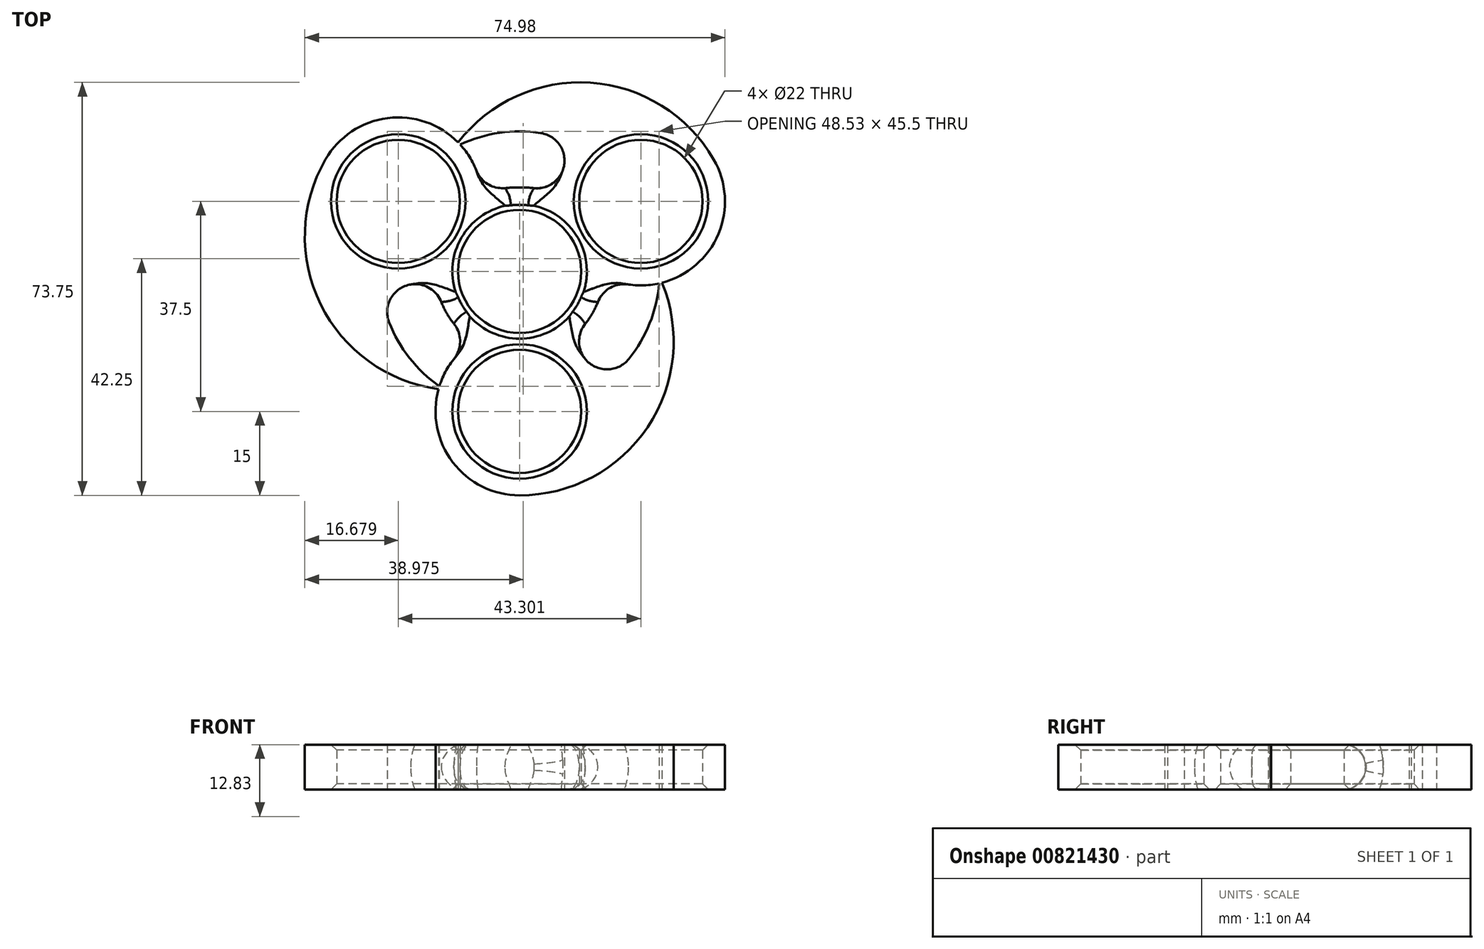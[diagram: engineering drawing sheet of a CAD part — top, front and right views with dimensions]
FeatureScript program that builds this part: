
annotation { "Feature Type Name" : "Feature", "Feature Type Description" : "" }
export const myFeature = defineFeature(function(context is Context, id is Id, definition is map)
    precondition{}
    {
        {
            var Q0;
            Q0=qCreatedBy(makeId("Top.planeOp"),FACE);
            var sketch = newSketch(context, id + "F0", { "sketchPlane" : qUnion([Q0])});
            skCircle(sketch, "E0", {"center": v(0, 0) * mm, "radius": 15 * mm});
            skCircle(sketch, "E1", {"center": v(0, 0) * mm, "radius": 25 * mm, "construction": true});
            skLineSegment(sketch, "E2", {"start": v(0, 56.43) * mm, "end": v(0, 0) * mm});
            skLineSegment(sketch, "E3", {"start": v(0, 0) * mm, "end": v(21.65, 12.5) * mm});
            skLineSegment(sketch, "E4", {"start": v(0, 0) * mm, "end": v(-21.65, 12.5) * mm});
            skLineSegment(sketch, "E5", {"start": v(0, 0) * mm, "end": v(0, -25) * mm});
            skCircle(sketch, "E6", {"center": v(-21.65, 12.5) * mm, "radius": 11 * mm});
            skCircle(sketch, "E7", {"center": v(21.65, 12.5) * mm, "radius": 11 * mm});
            skCircle(sketch, "E8", {"center": v(0, -25) * mm, "radius": 11 * mm});
            skCircle(sketch, "E9", {"center": v(-21.65, 12.5) * mm, "radius": 15 * mm});
            skCircle(sketch, "E10", {"center": v(21.65, 12.5) * mm, "radius": 15 * mm});
            skCircle(sketch, "E11", {"center": v(0, -25) * mm, "radius": 15 * mm});
            skCircle(sketch, "E12", {"center": v(0, 0) * mm, "radius": 11 * mm});
            skCircle(sketch, "E13", {"center": v(-10.83, 6.25) * mm, "radius": 27.5 * mm});
            skCircle(sketch, "E14", {"center": v(10.83, 6.25) * mm, "radius": 27.5 * mm});
            skCircle(sketch, "E15", {"center": v(0, -12.5) * mm, "radius": 27.5 * mm});
            skCircle(sketch, "E16", {"center": v(0, 15) * mm, "radius": 32.8 * mm});
            skCircle(sketch, "E17", {"center": v(0, -15) * mm, "radius": 46 * mm});
            skCircle(sketch, "E18", {"center": v(12.12, 7) * mm, "radius": 45.22 * mm});
            skCircle(sketch, "E19", {"center": v(0, 0) * mm, "radius": 25 * mm});
            skSolve(sketch);
        }
        {
            var Q0;
            {var subQ3=sQuery(id+"F0.wireOp",EDGE,"E19");var subQ6=sQuery(id+"F0.wireOp",EDGE,"E8");var subQ9=makeQuery(id+"F0.imprint","INTERSECT",VERTEX,{"disambiguationData":[OD(1.0)],"derivedFrom":[subQ6,subQ3]});Q0=makeQuery(id+"F0.imprint","IMPRINT",FACE,{"disambiguationData":[TD([[makeQuery(id+"F0.imprint","IMPRINT",EDGE,{"disambiguationData":[TD([[subQ9,-1.0]])],"derivedFrom":subQ6}),-1.0]])]});}
            var Q1;
            {var subQ0=sQuery(id+"F0.wireOp",EDGE,"E13");var subQ1=sQuery(id+"F0.wireOp",EDGE,"E8");var subQ2=makeQuery(id+"F0.imprint","INTERSECT",VERTEX,{"disambiguationData":[OD(1.0)],"derivedFrom":[subQ1,subQ0]});Q1=makeQuery(id+"F0.imprint","IMPRINT",FACE,{"disambiguationData":[TD([[makeQuery(id+"F0.imprint","IMPRINT",EDGE,{"disambiguationData":[TD([[subQ2,-1.0]])],"derivedFrom":subQ1}),-1.0]])]});}
            var Q2;
            {var subQ0=sQuery(id+"F0.wireOp",EDGE,"E16");var subQ1=sQuery(id+"F0.wireOp",EDGE,"E8");var subQ2=makeQuery(id+"F0.imprint","INTERSECT",VERTEX,{"disambiguationData":[OD(1.0)],"derivedFrom":[subQ1,subQ0]});Q2=makeQuery(id+"F0.imprint","IMPRINT",FACE,{"disambiguationData":[TD([[makeQuery(id+"F0.imprint","IMPRINT",EDGE,{"disambiguationData":[TD([[subQ2,-1.0]])],"derivedFrom":subQ1}),-1.0]])]});}
            var Q3;
            {var subQ0=sQuery(id+"F0.wireOp",EDGE,"E19");var subQ1=sQuery(id+"F0.wireOp",EDGE,"E11");var subQ2=makeQuery(id+"F0.imprint","INTERSECT",VERTEX,{"disambiguationData":[OD(1.0)],"derivedFrom":[subQ1,subQ0]});Q3=makeQuery(id+"F0.imprint","IMPRINT",FACE,{"disambiguationData":[TD([[makeQuery(id+"F0.imprint","IMPRINT",EDGE,{"disambiguationData":[TD([[subQ2,-1.0]])],"derivedFrom":subQ1}),1.0]])]});}
            var Q4;
            {var subQ0=sQuery(id+"F0.wireOp",EDGE,"E14");var subQ1=sQuery(id+"F0.wireOp",EDGE,"E8");var subQ2=makeQuery(id+"F0.imprint","INTERSECT",VERTEX,{"disambiguationData":[OD(1.0)],"derivedFrom":[subQ1,subQ0]});Q4=makeQuery(id+"F0.imprint","IMPRINT",FACE,{"disambiguationData":[TD([[makeQuery(id+"F0.imprint","IMPRINT",EDGE,{"disambiguationData":[TD([[subQ2,-1.0]])],"derivedFrom":subQ1}),-1.0]])]});}
            var Q5;
            {var subQ0=sQuery(id+"F0.wireOp",EDGE,"E11");var subQ1=sQuery(id+"F0.wireOp",EDGE,"E0");var subQ2=makeQuery(id+"F0.imprint","INTERSECT",VERTEX,{"disambiguationData":[OD(0.0)],"derivedFrom":[subQ1,subQ0]});Q5=makeQuery(id+"F0.imprint","IMPRINT",FACE,{"disambiguationData":[TD([[makeQuery(id+"F0.imprint","IMPRINT",EDGE,{"disambiguationData":[TD([[subQ2,-1.0]])],"derivedFrom":subQ1}),-1.0]])]});}
            var Q6;
            {var subQ0=sQuery(id+"F0.wireOp",EDGE,"E11");var subQ1=sQuery(id+"F0.wireOp",EDGE,"E0");var subQ2=makeQuery(id+"F0.imprint","INTERSECT",VERTEX,{"disambiguationData":[OD(0.0)],"derivedFrom":[subQ1,subQ0]});Q6=makeQuery(id+"F0.imprint","IMPRINT",FACE,{"disambiguationData":[TD([[makeQuery(id+"F0.imprint","IMPRINT",EDGE,{"disambiguationData":[TD([[subQ2,-1.0]])],"derivedFrom":subQ1}),1.0]])]});}
            var Q7;
            {var subQ1=sQuery(id+"F0.wireOp",EDGE,"E0");var subQ5=sQuery(id+"F0.wireOp",EDGE,"E8");var subQ6=makeQuery(id+"F0.imprint","INTERSECT",VERTEX,{"disambiguationData":[OD(1.0)],"derivedFrom":[subQ1,subQ5]});Q7=makeQuery(id+"F0.imprint","IMPRINT",FACE,{"disambiguationData":[TD([[makeQuery(id+"F0.imprint","IMPRINT",EDGE,{"disambiguationData":[TD([[subQ6,-1.0]])],"derivedFrom":subQ1}),1.0]])]});}
            var Q8;
            {var subQ0=sQuery(id+"F0.wireOp",EDGE,"E16");var subQ1=sQuery(id+"F0.wireOp",EDGE,"E8");var subQ2=makeQuery(id+"F0.imprint","INTERSECT",VERTEX,{"disambiguationData":[OD(0.0)],"derivedFrom":[subQ1,subQ0]});Q8=makeQuery(id+"F0.imprint","IMPRINT",FACE,{"disambiguationData":[TD([[makeQuery(id+"F0.imprint","IMPRINT",EDGE,{"disambiguationData":[TD([[subQ2,-1.0]])],"derivedFrom":subQ1}),-1.0]])]});}
            var Q9;
            {var subQ0=sQuery(id+"F0.wireOp",EDGE,"E8");var subQ1=sQuery(id+"F0.wireOp",EDGE,"E0");var subQ2=makeQuery(id+"F0.imprint","INTERSECT",VERTEX,{"disambiguationData":[OD(1.0)],"derivedFrom":[subQ1,subQ0]});Q9=makeQuery(id+"F0.imprint","IMPRINT",FACE,{"disambiguationData":[TD([[makeQuery(id+"F0.imprint","IMPRINT",EDGE,{"disambiguationData":[TD([[subQ2,-1.0]])],"derivedFrom":subQ1}),-1.0]])]});}
            var Q10;
            {var subQ0=sQuery(id+"F0.wireOp",EDGE,"E14");var subQ1=sQuery(id+"F0.wireOp",EDGE,"E8");var subQ2=makeQuery(id+"F0.imprint","INTERSECT",VERTEX,{"disambiguationData":[OD(0.0)],"derivedFrom":[subQ1,subQ0]});Q10=makeQuery(id+"F0.imprint","IMPRINT",FACE,{"disambiguationData":[TD([[makeQuery(id+"F0.imprint","IMPRINT",EDGE,{"disambiguationData":[TD([[subQ2,-1.0]])],"derivedFrom":subQ1}),-1.0]])]});}
            var Q11;
            {var subQ0=sQuery(id+"F0.wireOp",EDGE,"E14");var subQ1=sQuery(id+"F0.wireOp",EDGE,"E8");var subQ2=makeQuery(id+"F0.imprint","INTERSECT",VERTEX,{"disambiguationData":[OD(0.0)],"derivedFrom":[subQ1,subQ0]});Q11=makeQuery(id+"F0.imprint","IMPRINT",FACE,{"disambiguationData":[TD([[makeQuery(id+"F0.imprint","IMPRINT",EDGE,{"disambiguationData":[TD([[subQ2,1.0]])],"derivedFrom":subQ1}),-1.0]])]});}
            var Q12;
            {var subQ1=sQuery(id+"F0.wireOp",EDGE,"E8");var subQ5=sQuery(id+"F0.wireOp",EDGE,"E19");var subQ6=makeQuery(id+"F0.imprint","INTERSECT",VERTEX,{"disambiguationData":[OD(0.0)],"derivedFrom":[subQ1,subQ5]});Q12=makeQuery(id+"F0.imprint","IMPRINT",FACE,{"disambiguationData":[TD([[makeQuery(id+"F0.imprint","IMPRINT",EDGE,{"disambiguationData":[TD([[subQ6,1.0]])],"derivedFrom":subQ1}),-1.0]])]});}
            var Q13;
            {var subQ0=sQuery(id+"F0.wireOp",EDGE,"E18");var subQ1=sQuery(id+"F0.wireOp",EDGE,"E11");var subQ2=makeQuery(id+"F0.imprint","INTERSECT",VERTEX,{"disambiguationData":[OD(0.0)],"derivedFrom":[subQ1,subQ0]});Q13=makeQuery(id+"F0.imprint","IMPRINT",FACE,{"disambiguationData":[TD([[makeQuery(id+"F0.imprint","IMPRINT",EDGE,{"disambiguationData":[TD([[subQ2,-1.0]])],"derivedFrom":subQ1}),1.0]])]});}
            var Q14;
            {var subQ0=sQuery(id+"F0.wireOp",EDGE,"E19");var subQ1=sQuery(id+"F0.wireOp",EDGE,"E11");var subQ2=makeQuery(id+"F0.imprint","INTERSECT",VERTEX,{"disambiguationData":[OD(0.0)],"derivedFrom":[subQ1,subQ0]});Q14=makeQuery(id+"F0.imprint","IMPRINT",FACE,{"disambiguationData":[TD([[makeQuery(id+"F0.imprint","IMPRINT",EDGE,{"disambiguationData":[TD([[subQ2,1.0]])],"derivedFrom":subQ1}),1.0]])]});}
            var Q15;
            {var subQ0=sQuery(id+"F0.wireOp",EDGE,"E14");var subQ1=sQuery(id+"F0.wireOp",EDGE,"E11");var subQ2=makeQuery(id+"F0.imprint","INTERSECT",VERTEX,{"disambiguationData":[OD(0.0)],"derivedFrom":[subQ1,subQ0]});Q15=makeQuery(id+"F0.imprint","IMPRINT",FACE,{"disambiguationData":[TD([[makeQuery(id+"F0.imprint","IMPRINT",EDGE,{"disambiguationData":[TD([[subQ2,1.0]])],"derivedFrom":subQ1}),-1.0]])]});}
            var Q16;
            {var subQ3=sQuery(id+"F0.wireOp",EDGE,"E19");var subQ7=sQuery(id+"F0.wireOp",EDGE,"E11");var subQ9=makeQuery(id+"F0.imprint","INTERSECT",VERTEX,{"disambiguationData":[OD(0.0)],"derivedFrom":[subQ7,subQ3]});Q16=makeQuery(id+"F0.imprint","IMPRINT",FACE,{"disambiguationData":[TD([[makeQuery(id+"F0.imprint","IMPRINT",EDGE,{"disambiguationData":[TD([[subQ9,1.0]])],"derivedFrom":subQ7}),-1.0]])]});}
            var Q17;
            {var subQ0=sQuery(id+"F0.wireOp",EDGE,"E19");var subQ1=sQuery(id+"F0.wireOp",EDGE,"E10");var subQ2=makeQuery(id+"F0.imprint","INTERSECT",VERTEX,{"disambiguationData":[OD(1.0)],"derivedFrom":[subQ1,subQ0]});Q17=makeQuery(id+"F0.imprint","IMPRINT",FACE,{"disambiguationData":[TD([[makeQuery(id+"F0.imprint","IMPRINT",EDGE,{"disambiguationData":[TD([[subQ2,-1.0]])],"derivedFrom":subQ1}),-1.0]])]});}
            var Q18;
            {var subQ0=sQuery(id+"F0.wireOp",EDGE,"E13");var subQ1=sQuery(id+"F0.wireOp",EDGE,"E7");var subQ2=makeQuery(id+"F0.imprint","INTERSECT",VERTEX,{"disambiguationData":[OD(1.0)],"derivedFrom":[subQ1,subQ0]});Q18=makeQuery(id+"F0.imprint","IMPRINT",FACE,{"disambiguationData":[TD([[makeQuery(id+"F0.imprint","IMPRINT",EDGE,{"disambiguationData":[TD([[subQ2,-1.0]])],"derivedFrom":subQ1}),-1.0]])]});}
            var Q19;
            {var subQ0=sQuery(id+"F0.wireOp",EDGE,"E19");var subQ1=sQuery(id+"F0.wireOp",EDGE,"E10");var subQ2=makeQuery(id+"F0.imprint","INTERSECT",VERTEX,{"disambiguationData":[OD(1.0)],"derivedFrom":[subQ1,subQ0]});Q19=makeQuery(id+"F0.imprint","IMPRINT",FACE,{"disambiguationData":[TD([[makeQuery(id+"F0.imprint","IMPRINT",EDGE,{"disambiguationData":[TD([[subQ2,-1.0]])],"derivedFrom":subQ1}),1.0]])]});}
            var Q20;
            {var subQ0=sQuery(id+"F0.wireOp",EDGE,"E15");var subQ1=sQuery(id+"F0.wireOp",EDGE,"E7");var subQ2=makeQuery(id+"F0.imprint","INTERSECT",VERTEX,{"disambiguationData":[OD(1.0)],"derivedFrom":[subQ1,subQ0]});Q20=makeQuery(id+"F0.imprint","IMPRINT",FACE,{"disambiguationData":[TD([[makeQuery(id+"F0.imprint","IMPRINT",EDGE,{"disambiguationData":[TD([[subQ2,-1.0]])],"derivedFrom":subQ1}),-1.0]])]});}
            var Q21;
            {var subQ0=sQuery(id+"F0.wireOp",EDGE,"E11");var subQ1=sQuery(id+"F0.wireOp",EDGE,"E0");var subQ2=makeQuery(id+"F0.imprint","INTERSECT",VERTEX,{"disambiguationData":[OD(1.0)],"derivedFrom":[subQ1,subQ0]});Q21=makeQuery(id+"F0.imprint","IMPRINT",FACE,{"disambiguationData":[TD([[makeQuery(id+"F0.imprint","IMPRINT",EDGE,{"disambiguationData":[TD([[subQ2,-1.0]])],"derivedFrom":subQ1}),1.0]])]});}
            var Q22;
            {var subQ0=sQuery(id+"F0.wireOp",EDGE,"E7");var subQ1=sQuery(id+"F0.wireOp",EDGE,"E0");var subQ2=makeQuery(id+"F0.imprint","INTERSECT",VERTEX,{"disambiguationData":[OD(0.0)],"derivedFrom":[subQ1,subQ0]});Q22=makeQuery(id+"F0.imprint","IMPRINT",FACE,{"disambiguationData":[TD([[makeQuery(id+"F0.imprint","IMPRINT",EDGE,{"disambiguationData":[TD([[subQ2,1.0]])],"derivedFrom":subQ1}),1.0]])]});}
            var Q23;
            {var subQ0=sQuery(id+"F0.wireOp",EDGE,"E7");var subQ1=sQuery(id+"F0.wireOp",EDGE,"E0");var subQ2=makeQuery(id+"F0.imprint","INTERSECT",VERTEX,{"disambiguationData":[OD(0.0)],"derivedFrom":[subQ1,subQ0]});Q23=makeQuery(id+"F0.imprint","IMPRINT",FACE,{"disambiguationData":[TD([[makeQuery(id+"F0.imprint","IMPRINT",EDGE,{"disambiguationData":[TD([[subQ2,1.0]])],"derivedFrom":subQ1}),-1.0]])]});}
            var Q24;
            {var subQ1=sQuery(id+"F0.wireOp",EDGE,"E0");var subQ5=sQuery(id+"F0.wireOp",EDGE,"E7");var subQ6=makeQuery(id+"F0.imprint","INTERSECT",VERTEX,{"disambiguationData":[OD(1.0)],"derivedFrom":[subQ1,subQ5]});Q24=makeQuery(id+"F0.imprint","IMPRINT",FACE,{"disambiguationData":[TD([[makeQuery(id+"F0.imprint","IMPRINT",EDGE,{"disambiguationData":[TD([[subQ6,-1.0]])],"derivedFrom":subQ1}),1.0]])]});}
            var Q25;
            {var subQ0=sQuery(id+"F0.wireOp",EDGE,"E7");var subQ1=sQuery(id+"F0.wireOp",EDGE,"E0");var subQ2=makeQuery(id+"F0.imprint","INTERSECT",VERTEX,{"disambiguationData":[OD(1.0)],"derivedFrom":[subQ1,subQ0]});Q25=makeQuery(id+"F0.imprint","IMPRINT",FACE,{"disambiguationData":[TD([[makeQuery(id+"F0.imprint","IMPRINT",EDGE,{"disambiguationData":[TD([[subQ2,-1.0]])],"derivedFrom":subQ1}),-1.0]])]});}
            var Q26;
            {var subQ1=sQuery(id+"F0.wireOp",EDGE,"E7");var subQ5=sQuery(id+"F0.wireOp",EDGE,"E13");var subQ6=makeQuery(id+"F0.imprint","INTERSECT",VERTEX,{"disambiguationData":[OD(0.0)],"derivedFrom":[subQ1,subQ5]});Q26=makeQuery(id+"F0.imprint","IMPRINT",FACE,{"disambiguationData":[TD([[makeQuery(id+"F0.imprint","IMPRINT",EDGE,{"disambiguationData":[TD([[subQ6,-1.0]])],"derivedFrom":subQ1}),-1.0]])]});}
            var Q27;
            {var subQ1=sQuery(id+"F0.wireOp",EDGE,"E7");var subQ5=sQuery(id+"F0.wireOp",EDGE,"E19");var subQ6=makeQuery(id+"F0.imprint","INTERSECT",VERTEX,{"disambiguationData":[OD(1.0)],"derivedFrom":[subQ1,subQ5]});Q27=makeQuery(id+"F0.imprint","IMPRINT",FACE,{"disambiguationData":[TD([[makeQuery(id+"F0.imprint","IMPRINT",EDGE,{"disambiguationData":[TD([[subQ6,-1.0]])],"derivedFrom":subQ1}),-1.0]])]});}
            var Q28;
            {var subQ0=sQuery(id+"F0.wireOp",EDGE,"E17");var subQ1=sQuery(id+"F0.wireOp",EDGE,"E10");var subQ2=makeQuery(id+"F0.imprint","INTERSECT",VERTEX,{"disambiguationData":[OD(0.0)],"derivedFrom":[subQ1,subQ0]});Q28=makeQuery(id+"F0.imprint","IMPRINT",FACE,{"disambiguationData":[TD([[makeQuery(id+"F0.imprint","IMPRINT",EDGE,{"disambiguationData":[TD([[subQ2,1.0]])],"derivedFrom":subQ1}),1.0]])]});}
            var Q29;
            {var subQ1=sQuery(id+"F0.wireOp",EDGE,"E7");var subQ7=sQuery(id+"F0.wireOp",EDGE,"E19");var subQ8=makeQuery(id+"F0.imprint","INTERSECT",VERTEX,{"disambiguationData":[OD(0.0)],"derivedFrom":[subQ1,subQ7]});Q29=makeQuery(id+"F0.imprint","IMPRINT",FACE,{"disambiguationData":[TD([[makeQuery(id+"F0.imprint","IMPRINT",EDGE,{"disambiguationData":[TD([[subQ8,1.0]])],"derivedFrom":subQ1}),-1.0]])]});}
            var Q30;
            {var subQ0=sQuery(id+"F0.wireOp",EDGE,"E16");var subQ1=sQuery(id+"F0.wireOp",EDGE,"E10");var subQ2=makeQuery(id+"F0.imprint","INTERSECT",VERTEX,{"disambiguationData":[OD(0.0)],"derivedFrom":[subQ1,subQ0]});Q30=makeQuery(id+"F0.imprint","IMPRINT",FACE,{"disambiguationData":[TD([[makeQuery(id+"F0.imprint","IMPRINT",EDGE,{"disambiguationData":[TD([[subQ2,-1.0]])],"derivedFrom":subQ1}),1.0]])]});}
            var Q31;
            {var subQ0=sQuery(id+"F0.wireOp",EDGE,"E10");var subQ1=makeQuery(id+"F0.imprint","INTERSECT",VERTEX,{"derivedFrom":[subQ0,sQuery(id+"F0.wireOp",EDGE,"E14")]});Q31=makeQuery(id+"F0.imprint","IMPRINT",FACE,{"disambiguationData":[TD([[makeQuery(id+"F0.imprint","IMPRINT",EDGE,{"disambiguationData":[TD([[subQ1,1.0]])],"derivedFrom":subQ0}),1.0]])]});}
            var Q32;
            {var subQ0=sQuery(id+"F0.wireOp",EDGE,"E17");var subQ1=sQuery(id+"F0.wireOp",EDGE,"E7");var subQ2=makeQuery(id+"F0.imprint","INTERSECT",VERTEX,{"derivedFrom":[subQ1,subQ0]});Q32=makeQuery(id+"F0.imprint","IMPRINT",FACE,{"disambiguationData":[TD([[makeQuery(id+"F0.imprint","IMPRINT",EDGE,{"disambiguationData":[TD([[subQ2,1.0]])],"derivedFrom":subQ1}),-1.0]])]});}
            var Q33;
            {var subQ0=sQuery(id+"F0.wireOp",EDGE,"E19");var subQ1=sQuery(id+"F0.wireOp",EDGE,"E7");var subQ2=makeQuery(id+"F0.imprint","INTERSECT",VERTEX,{"disambiguationData":[OD(0.0)],"derivedFrom":[subQ1,subQ0]});Q33=makeQuery(id+"F0.imprint","IMPRINT",FACE,{"disambiguationData":[TD([[makeQuery(id+"F0.imprint","IMPRINT",EDGE,{"disambiguationData":[TD([[subQ2,-1.0]])],"derivedFrom":subQ1}),-1.0]])]});}
            var Q34;
            {var subQ0=sQuery(id+"F0.wireOp",EDGE,"E13");var subQ1=sQuery(id+"F0.wireOp",EDGE,"E10");var subQ2=makeQuery(id+"F0.imprint","INTERSECT",VERTEX,{"disambiguationData":[OD(0.0)],"derivedFrom":[subQ1,subQ0]});Q34=makeQuery(id+"F0.imprint","IMPRINT",FACE,{"disambiguationData":[TD([[makeQuery(id+"F0.imprint","IMPRINT",EDGE,{"disambiguationData":[TD([[subQ2,-1.0]])],"derivedFrom":subQ1}),1.0]])]});}
            var Q35;
            {var subQ0=sQuery(id+"F0.wireOp",EDGE,"E10");var subQ1=sQuery(id+"F0.wireOp",EDGE,"E0");var subQ2=makeQuery(id+"F0.imprint","INTERSECT",VERTEX,{"disambiguationData":[OD(0.0)],"derivedFrom":[subQ1,subQ0]});Q35=makeQuery(id+"F0.imprint","IMPRINT",FACE,{"disambiguationData":[TD([[makeQuery(id+"F0.imprint","IMPRINT",EDGE,{"disambiguationData":[TD([[subQ2,-1.0]])],"derivedFrom":subQ0}),-1.0]])]});}
            var Q36;
            {var subQ0=sQuery(id+"F0.wireOp",EDGE,"E9");var subQ1=sQuery(id+"F0.wireOp",EDGE,"E0");var subQ2=makeQuery(id+"F0.imprint","INTERSECT",VERTEX,{"disambiguationData":[OD(0.0)],"derivedFrom":[subQ1,subQ0]});Q36=makeQuery(id+"F0.imprint","IMPRINT",FACE,{"disambiguationData":[TD([[makeQuery(id+"F0.imprint","IMPRINT",EDGE,{"disambiguationData":[TD([[subQ2,1.0]])],"derivedFrom":subQ0}),-1.0]])]});}
            var Q37;
            {var subQ0=sQuery(id+"F0.wireOp",EDGE,"E16");var subQ1=sQuery(id+"F0.wireOp",EDGE,"E10");var subQ2=makeQuery(id+"F0.imprint","INTERSECT",VERTEX,{"disambiguationData":[OD(0.0)],"derivedFrom":[subQ1,subQ0]});Q37=makeQuery(id+"F0.imprint","IMPRINT",FACE,{"disambiguationData":[TD([[makeQuery(id+"F0.imprint","IMPRINT",EDGE,{"disambiguationData":[TD([[subQ2,-1.0]])],"derivedFrom":subQ1}),-1.0]])]});}
            var Q38;
            {var subQ5=sQuery(id+"F0.wireOp",EDGE,"E17");var subQ7=sQuery(id+"F0.wireOp",EDGE,"E9");var subQ9=makeQuery(id+"F0.imprint","INTERSECT",VERTEX,{"disambiguationData":[OD(1.0)],"derivedFrom":[subQ7,subQ5]});Q38=makeQuery(id+"F0.imprint","IMPRINT",FACE,{"disambiguationData":[TD([[makeQuery(id+"F0.imprint","IMPRINT",EDGE,{"disambiguationData":[TD([[subQ9,-1.0]])],"derivedFrom":subQ7}),-1.0]])]});}
            var Q39;
            {var subQ0=sQuery(id+"F0.wireOp",EDGE,"E18");var subQ1=sQuery(id+"F0.wireOp",EDGE,"E9");var subQ2=makeQuery(id+"F0.imprint","INTERSECT",VERTEX,{"disambiguationData":[OD(0.0)],"derivedFrom":[subQ1,subQ0]});Q39=makeQuery(id+"F0.imprint","IMPRINT",FACE,{"disambiguationData":[TD([[makeQuery(id+"F0.imprint","IMPRINT",EDGE,{"disambiguationData":[TD([[subQ2,-1.0]])],"derivedFrom":subQ1}),1.0]])]});}
            var Q40;
            {var subQ0=sQuery(id+"F0.wireOp",EDGE,"E17");var subQ1=sQuery(id+"F0.wireOp",EDGE,"E9");var subQ2=makeQuery(id+"F0.imprint","INTERSECT",VERTEX,{"disambiguationData":[OD(0.0)],"derivedFrom":[subQ1,subQ0]});Q40=makeQuery(id+"F0.imprint","IMPRINT",FACE,{"disambiguationData":[TD([[makeQuery(id+"F0.imprint","IMPRINT",EDGE,{"disambiguationData":[TD([[subQ2,-1.0]])],"derivedFrom":subQ1}),1.0]])]});}
            var Q41;
            {var subQ1=sQuery(id+"F0.wireOp",EDGE,"E6");var subQ5=sQuery(id+"F0.wireOp",EDGE,"E19");var subQ6=makeQuery(id+"F0.imprint","INTERSECT",VERTEX,{"disambiguationData":[OD(0.0)],"derivedFrom":[subQ1,subQ5]});Q41=makeQuery(id+"F0.imprint","IMPRINT",FACE,{"disambiguationData":[TD([[makeQuery(id+"F0.imprint","IMPRINT",EDGE,{"disambiguationData":[TD([[subQ6,-1.0]])],"derivedFrom":subQ1}),-1.0]])]});}
            var Q42;
            {var subQ0=sQuery(id+"F0.wireOp",EDGE,"E14");var subQ1=sQuery(id+"F0.wireOp",EDGE,"E6");var subQ2=makeQuery(id+"F0.imprint","INTERSECT",VERTEX,{"disambiguationData":[OD(0.0)],"derivedFrom":[subQ1,subQ0]});Q42=makeQuery(id+"F0.imprint","IMPRINT",FACE,{"disambiguationData":[TD([[makeQuery(id+"F0.imprint","IMPRINT",EDGE,{"disambiguationData":[TD([[subQ2,-1.0]])],"derivedFrom":subQ1}),-1.0]])]});}
            var Q43;
            {var subQ0=sQuery(id+"F0.wireOp",EDGE,"E14");var subQ1=sQuery(id+"F0.wireOp",EDGE,"E6");var subQ2=makeQuery(id+"F0.imprint","INTERSECT",VERTEX,{"disambiguationData":[OD(0.0)],"derivedFrom":[subQ1,subQ0]});Q43=makeQuery(id+"F0.imprint","IMPRINT",FACE,{"disambiguationData":[TD([[makeQuery(id+"F0.imprint","IMPRINT",EDGE,{"disambiguationData":[TD([[subQ2,1.0]])],"derivedFrom":subQ1}),-1.0]])]});}
            var Q44;
            {var subQ0=sQuery(id+"F0.wireOp",EDGE,"E19");var subQ1=sQuery(id+"F0.wireOp",EDGE,"E9");var subQ2=makeQuery(id+"F0.imprint","INTERSECT",VERTEX,{"disambiguationData":[OD(0.0)],"derivedFrom":[subQ1,subQ0]});Q44=makeQuery(id+"F0.imprint","IMPRINT",FACE,{"disambiguationData":[TD([[makeQuery(id+"F0.imprint","IMPRINT",EDGE,{"disambiguationData":[TD([[subQ2,-1.0]])],"derivedFrom":subQ1}),1.0]])]});}
            var Q45;
            {var subQ0=sQuery(id+"F0.wireOp",EDGE,"E9");var subQ1=sQuery(id+"F0.wireOp",EDGE,"E0");var subQ2=makeQuery(id+"F0.imprint","INTERSECT",VERTEX,{"disambiguationData":[OD(0.0)],"derivedFrom":[subQ1,subQ0]});Q45=makeQuery(id+"F0.imprint","IMPRINT",FACE,{"disambiguationData":[TD([[makeQuery(id+"F0.imprint","IMPRINT",EDGE,{"disambiguationData":[TD([[subQ2,-1.0]])],"derivedFrom":subQ1}),-1.0]])]});}
            var Q46;
            {var subQ0=sQuery(id+"F0.wireOp",EDGE,"E9");var subQ1=sQuery(id+"F0.wireOp",EDGE,"E0");var subQ2=makeQuery(id+"F0.imprint","INTERSECT",VERTEX,{"disambiguationData":[OD(0.0)],"derivedFrom":[subQ1,subQ0]});Q46=makeQuery(id+"F0.imprint","IMPRINT",FACE,{"disambiguationData":[TD([[makeQuery(id+"F0.imprint","IMPRINT",EDGE,{"disambiguationData":[TD([[subQ2,-1.0]])],"derivedFrom":subQ0}),-1.0]])]});}
            var Q47;
            {var subQ0=sQuery(id+"F0.wireOp",EDGE,"E10");var subQ1=sQuery(id+"F0.wireOp",EDGE,"E0");var subQ2=makeQuery(id+"F0.imprint","INTERSECT",VERTEX,{"disambiguationData":[OD(0.0)],"derivedFrom":[subQ1,subQ0]});Q47=makeQuery(id+"F0.imprint","IMPRINT",FACE,{"disambiguationData":[TD([[makeQuery(id+"F0.imprint","IMPRINT",EDGE,{"disambiguationData":[TD([[subQ2,1.0]])],"derivedFrom":subQ0}),-1.0]])]});}
            var Q48;
            {var subQ0=sQuery(id+"F0.wireOp",EDGE,"E9");var subQ1=sQuery(id+"F0.wireOp",EDGE,"E0");var subQ2=makeQuery(id+"F0.imprint","INTERSECT",VERTEX,{"disambiguationData":[OD(0.0)],"derivedFrom":[subQ1,subQ0]});Q48=makeQuery(id+"F0.imprint","IMPRINT",FACE,{"disambiguationData":[TD([[makeQuery(id+"F0.imprint","IMPRINT",EDGE,{"disambiguationData":[TD([[subQ2,-1.0]])],"derivedFrom":subQ1}),1.0]])]});}
            var Q49;
            {var subQ0=sQuery(id+"F0.wireOp",EDGE,"E9");var subQ1=sQuery(id+"F0.wireOp",EDGE,"E0");var subQ2=makeQuery(id+"F0.imprint","INTERSECT",VERTEX,{"disambiguationData":[OD(1.0)],"derivedFrom":[subQ1,subQ0]});Q49=makeQuery(id+"F0.imprint","IMPRINT",FACE,{"disambiguationData":[TD([[makeQuery(id+"F0.imprint","IMPRINT",EDGE,{"disambiguationData":[TD([[subQ2,-1.0]])],"derivedFrom":subQ1}),1.0]])]});}
            var Q50;
            {var subQ1=sQuery(id+"F0.wireOp",EDGE,"E0");var subQ5=sQuery(id+"F0.wireOp",EDGE,"E6");var subQ6=makeQuery(id+"F0.imprint","INTERSECT",VERTEX,{"disambiguationData":[OD(1.0)],"derivedFrom":[subQ1,subQ5]});Q50=makeQuery(id+"F0.imprint","IMPRINT",FACE,{"disambiguationData":[TD([[makeQuery(id+"F0.imprint","IMPRINT",EDGE,{"disambiguationData":[TD([[subQ6,-1.0]])],"derivedFrom":subQ1}),1.0]])]});}
            var Q51;
            {var subQ0=sQuery(id+"F0.wireOp",EDGE,"E6");var subQ1=sQuery(id+"F0.wireOp",EDGE,"E0");var subQ2=makeQuery(id+"F0.imprint","INTERSECT",VERTEX,{"disambiguationData":[OD(1.0)],"derivedFrom":[subQ1,subQ0]});Q51=makeQuery(id+"F0.imprint","IMPRINT",FACE,{"disambiguationData":[TD([[makeQuery(id+"F0.imprint","IMPRINT",EDGE,{"disambiguationData":[TD([[subQ2,-1.0]])],"derivedFrom":subQ1}),-1.0]])]});}
            var Q52;
            {var subQ0=sQuery(id+"F0.wireOp",EDGE,"E15");var subQ1=sQuery(id+"F0.wireOp",EDGE,"E6");var subQ2=makeQuery(id+"F0.imprint","INTERSECT",VERTEX,{"disambiguationData":[OD(1.0)],"derivedFrom":[subQ1,subQ0]});Q52=makeQuery(id+"F0.imprint","IMPRINT",FACE,{"disambiguationData":[TD([[makeQuery(id+"F0.imprint","IMPRINT",EDGE,{"disambiguationData":[TD([[subQ2,-1.0]])],"derivedFrom":subQ1}),-1.0]])]});}
            var Q53;
            {var subQ0=sQuery(id+"F0.wireOp",EDGE,"E16");var subQ1=sQuery(id+"F0.wireOp",EDGE,"E6");var subQ2=makeQuery(id+"F0.imprint","INTERSECT",VERTEX,{"derivedFrom":[subQ1,subQ0]});Q53=makeQuery(id+"F0.imprint","IMPRINT",FACE,{"disambiguationData":[TD([[makeQuery(id+"F0.imprint","IMPRINT",EDGE,{"disambiguationData":[TD([[subQ2,-1.0]])],"derivedFrom":subQ1}),-1.0]])]});}
            var Q54;
            {var subQ0=sQuery(id+"F0.wireOp",EDGE,"E19");var subQ1=sQuery(id+"F0.wireOp",EDGE,"E6");var subQ2=makeQuery(id+"F0.imprint","INTERSECT",VERTEX,{"disambiguationData":[OD(1.0)],"derivedFrom":[subQ1,subQ0]});Q54=makeQuery(id+"F0.imprint","IMPRINT",FACE,{"disambiguationData":[TD([[makeQuery(id+"F0.imprint","IMPRINT",EDGE,{"disambiguationData":[TD([[subQ2,-1.0]])],"derivedFrom":subQ1}),-1.0]])]});}
            var Q55;
            {var subQ0=sQuery(id+"F0.wireOp",EDGE,"E15");var subQ1=sQuery(id+"F0.wireOp",EDGE,"E9");var subQ2=makeQuery(id+"F0.imprint","INTERSECT",VERTEX,{"disambiguationData":[OD(1.0)],"derivedFrom":[subQ1,subQ0]});Q55=makeQuery(id+"F0.imprint","IMPRINT",FACE,{"disambiguationData":[TD([[makeQuery(id+"F0.imprint","IMPRINT",EDGE,{"disambiguationData":[TD([[subQ2,-1.0]])],"derivedFrom":subQ1}),1.0]])]});}
            var Q56;
            {var subQ0=sQuery(id+"F0.wireOp",EDGE,"E17");var subQ1=sQuery(id+"F0.wireOp",EDGE,"E9");var subQ2=makeQuery(id+"F0.imprint","INTERSECT",VERTEX,{"disambiguationData":[OD(1.0)],"derivedFrom":[subQ1,subQ0]});Q56=makeQuery(id+"F0.imprint","IMPRINT",FACE,{"disambiguationData":[TD([[makeQuery(id+"F0.imprint","IMPRINT",EDGE,{"disambiguationData":[TD([[subQ2,-1.0]])],"derivedFrom":subQ1}),1.0]])]});}
            var Q57;
            {var subQ0=sQuery(id+"F0.wireOp",EDGE,"E18");var subQ1=sQuery(id+"F0.wireOp",EDGE,"E9");var subQ2=makeQuery(id+"F0.imprint","INTERSECT",VERTEX,{"disambiguationData":[OD(1.0)],"derivedFrom":[subQ1,subQ0]});Q57=makeQuery(id+"F0.imprint","IMPRINT",FACE,{"disambiguationData":[TD([[makeQuery(id+"F0.imprint","IMPRINT",EDGE,{"disambiguationData":[TD([[subQ2,-1.0]])],"derivedFrom":subQ1}),1.0]])]});}
            var Q58;
            {var subQ0=sQuery(id+"F0.wireOp",EDGE,"E17");var subQ1=sQuery(id+"F0.wireOp",EDGE,"E16");var subQ2=makeQuery(id+"F0.imprint","INTERSECT",VERTEX,{"disambiguationData":[OD(1.0)],"derivedFrom":[subQ1,subQ0]});Q58=makeQuery(id+"F0.imprint","IMPRINT",FACE,{"disambiguationData":[TD([[makeQuery(id+"F0.imprint","IMPRINT",EDGE,{"disambiguationData":[TD([[subQ2,-1.0]])],"derivedFrom":subQ1}),1.0]])]});}
            var Q59;
            {var subQ0=sQuery(id+"F0.wireOp",EDGE,"E9");var subQ1=makeQuery(id+"F0.imprint","INTERSECT",VERTEX,{"derivedFrom":[subQ0,sQuery(id+"F0.wireOp",EDGE,"E13")]});Q59=makeQuery(id+"F0.imprint","IMPRINT",FACE,{"disambiguationData":[TD([[makeQuery(id+"F0.imprint","IMPRINT",EDGE,{"disambiguationData":[TD([[subQ1,1.0]])],"derivedFrom":subQ0}),1.0]])]});}
            var Q60;
            {var subQ0=sQuery(id+"F0.wireOp",EDGE,"E13");var subQ1=sQuery(id+"F0.wireOp",EDGE,"E9");var subQ2=makeQuery(id+"F0.imprint","INTERSECT",VERTEX,{"derivedFrom":[subQ1,subQ0]});Q60=makeQuery(id+"F0.imprint","IMPRINT",FACE,{"disambiguationData":[TD([[makeQuery(id+"F0.imprint","IMPRINT",EDGE,{"disambiguationData":[TD([[subQ2,-1.0]])],"derivedFrom":subQ1}),-1.0]])]});}
            var Q61;
            {var subQ0=sQuery(id+"F0.wireOp",EDGE,"E17");var subQ1=sQuery(id+"F0.wireOp",EDGE,"E6");var subQ2=makeQuery(id+"F0.imprint","INTERSECT",VERTEX,{"derivedFrom":[subQ1,subQ0]});Q61=makeQuery(id+"F0.imprint","IMPRINT",FACE,{"disambiguationData":[TD([[makeQuery(id+"F0.imprint","IMPRINT",EDGE,{"disambiguationData":[TD([[subQ2,-1.0]])],"derivedFrom":subQ1}),-1.0]])]});}
            var Q62;
            {var subQ0=sQuery(id+"F0.wireOp",EDGE,"E15");var subQ1=sQuery(id+"F0.wireOp",EDGE,"E11");var subQ2=makeQuery(id+"F0.imprint","INTERSECT",VERTEX,{"derivedFrom":[subQ1,subQ0]});Q62=makeQuery(id+"F0.imprint","IMPRINT",FACE,{"disambiguationData":[TD([[makeQuery(id+"F0.imprint","IMPRINT",EDGE,{"disambiguationData":[TD([[subQ2,-1.0]])],"derivedFrom":subQ1}),-1.0]])]});}
            var Q63;
            {var subQ0=sQuery(id+"F0.wireOp",EDGE,"E17");var subQ1=sQuery(id+"F0.wireOp",EDGE,"E10");var subQ2=makeQuery(id+"F0.imprint","INTERSECT",VERTEX,{"disambiguationData":[OD(1.0)],"derivedFrom":[subQ1,subQ0]});Q63=makeQuery(id+"F0.imprint","IMPRINT",FACE,{"disambiguationData":[TD([[makeQuery(id+"F0.imprint","IMPRINT",EDGE,{"disambiguationData":[TD([[subQ2,-1.0]])],"derivedFrom":subQ1}),-1.0]])]});}
            var Q64;
            {var subQ0=sQuery(id+"F0.wireOp",EDGE,"E17");var subQ1=sQuery(id+"F0.wireOp",EDGE,"E2");var subQ2=makeQuery(id+"F0.imprint","INTERSECT",VERTEX,{"derivedFrom":[subQ1,subQ0]});Q64=makeQuery(id+"F0.imprint","IMPRINT",FACE,{"disambiguationData":[TD([[makeQuery(id+"F0.imprint","IMPRINT",EDGE,{"disambiguationData":[TD([[subQ2,-1.0]])],"derivedFrom":subQ1}),1.0]])]});}
            var Q65;
            {var subQ3=sQuery(id+"F0.wireOp",EDGE,"E17");var subQ5=sQuery(id+"F0.wireOp",EDGE,"E2");var subQ6=makeQuery(id+"F0.imprint","INTERSECT",VERTEX,{"derivedFrom":[subQ5,subQ3]});Q65=makeQuery(id+"F0.imprint","IMPRINT",FACE,{"disambiguationData":[TD([[makeQuery(id+"F0.imprint","IMPRINT",EDGE,{"disambiguationData":[TD([[subQ6,-1.0]])],"derivedFrom":subQ5}),-1.0]])]});}
            var Q66;
            {var subQ0=sQuery(id+"F0.wireOp",EDGE,"E18");var subQ1=sQuery(id+"F0.wireOp",EDGE,"E9");var subQ2=makeQuery(id+"F0.imprint","INTERSECT",VERTEX,{"disambiguationData":[OD(1.0)],"derivedFrom":[subQ1,subQ0]});Q66=makeQuery(id+"F0.imprint","IMPRINT",FACE,{"disambiguationData":[TD([[makeQuery(id+"F0.imprint","IMPRINT",EDGE,{"disambiguationData":[TD([[subQ2,-1.0]])],"derivedFrom":subQ1}),-1.0]])]});}
            var Q67;
            {var subQ3=sQuery(id+"F0.wireOp",EDGE,"E19");var subQ5=sQuery(id+"F0.wireOp",EDGE,"E11");var subQ6=makeQuery(id+"F0.imprint","INTERSECT",VERTEX,{"disambiguationData":[OD(1.0)],"derivedFrom":[subQ5,subQ3]});Q67=makeQuery(id+"F0.imprint","IMPRINT",FACE,{"disambiguationData":[TD([[makeQuery(id+"F0.imprint","IMPRINT",EDGE,{"disambiguationData":[TD([[subQ6,-1.0]])],"derivedFrom":subQ5}),-1.0]])]});}
            var Q68;
            {var subQ0=sQuery(id+"F0.wireOp",EDGE,"E16");var subQ1=sQuery(id+"F0.wireOp",EDGE,"E9");var subQ2=makeQuery(id+"F0.imprint","INTERSECT",VERTEX,{"disambiguationData":[OD(1.0)],"derivedFrom":[subQ1,subQ0]});Q68=makeQuery(id+"F0.imprint","IMPRINT",FACE,{"disambiguationData":[TD([[makeQuery(id+"F0.imprint","IMPRINT",EDGE,{"disambiguationData":[TD([[subQ2,-1.0]])],"derivedFrom":subQ1}),-1.0]])]});}
            var Q69;
            {var subQ0=sQuery(id+"F0.wireOp",EDGE,"E15");var subQ1=sQuery(id+"F0.wireOp",EDGE,"E9");var subQ2=makeQuery(id+"F0.imprint","INTERSECT",VERTEX,{"disambiguationData":[OD(1.0)],"derivedFrom":[subQ1,subQ0]});Q69=makeQuery(id+"F0.imprint","IMPRINT",FACE,{"disambiguationData":[TD([[makeQuery(id+"F0.imprint","IMPRINT",EDGE,{"disambiguationData":[TD([[subQ2,-1.0]])],"derivedFrom":subQ1}),-1.0]])]});}
            var Q70;
            {var subQ0=sQuery(id+"F0.wireOp",EDGE,"E14");var subQ1=sQuery(id+"F0.wireOp",EDGE,"E10");var subQ2=makeQuery(id+"F0.imprint","INTERSECT",VERTEX,{"derivedFrom":[subQ1,subQ0]});Q70=makeQuery(id+"F0.imprint","IMPRINT",FACE,{"disambiguationData":[TD([[makeQuery(id+"F0.imprint","IMPRINT",EDGE,{"disambiguationData":[TD([[subQ2,-1.0]])],"derivedFrom":subQ1}),-1.0]])]});}
            var Q71;
            {var subQ0=sQuery(id+"F0.wireOp",EDGE,"E17");var subQ1=sQuery(id+"F0.wireOp",EDGE,"E2");var subQ2=makeQuery(id+"F0.imprint","INTERSECT",VERTEX,{"derivedFrom":[subQ1,subQ0]});Q71=makeQuery(id+"F0.imprint","IMPRINT",FACE,{"disambiguationData":[TD([[makeQuery(id+"F0.imprint","IMPRINT",EDGE,{"disambiguationData":[TD([[subQ2,-1.0]])],"derivedFrom":subQ0}),-1.0]])]});}
            var Q72;
            {var subQ0=sQuery(id+"F0.wireOp",EDGE,"E17");var subQ1=sQuery(id+"F0.wireOp",EDGE,"E2");var subQ2=makeQuery(id+"F0.imprint","INTERSECT",VERTEX,{"derivedFrom":[subQ1,subQ0]});Q72=makeQuery(id+"F0.imprint","IMPRINT",FACE,{"disambiguationData":[TD([[makeQuery(id+"F0.imprint","IMPRINT",EDGE,{"disambiguationData":[TD([[subQ2,1.0]])],"derivedFrom":subQ0}),-1.0]])]});}
            var Q73;
            {var subQ0=sQuery(id+"F0.wireOp",EDGE,"E15");var subQ1=sQuery(id+"F0.wireOp",EDGE,"E13");var subQ2=makeQuery(id+"F0.imprint","INTERSECT",VERTEX,{"derivedFrom":[subQ1,subQ0]});Q73=makeQuery(id+"F0.imprint","IMPRINT",FACE,{"disambiguationData":[TD([[makeQuery(id+"F0.imprint","IMPRINT",EDGE,{"disambiguationData":[TD([[subQ2,-1.0]])],"derivedFrom":subQ1}),1.0]])]});}
            var Q74;
            {var subQ0=sQuery(id+"F0.wireOp",EDGE,"E18");var subQ1=sQuery(id+"F0.wireOp",EDGE,"E6");var subQ2=makeQuery(id+"F0.imprint","INTERSECT",VERTEX,{"derivedFrom":[subQ1,subQ0]});Q74=makeQuery(id+"F0.imprint","IMPRINT",FACE,{"disambiguationData":[TD([[makeQuery(id+"F0.imprint","IMPRINT",EDGE,{"disambiguationData":[TD([[subQ2,-1.0]])],"derivedFrom":subQ1}),-1.0]])]});}
            extrude(context, id + "F1", {"entities" : qUnion([Q0, Q1, Q2, Q3, Q4, Q5, Q6, Q7, Q8, Q9, Q10, Q11, Q12, Q13, Q14, Q15, Q16, Q17, Q18, Q19, Q20, Q21, Q22, Q23, Q24, Q25, Q26, Q27, Q28, Q29, Q30, Q31, Q32, Q33, Q34, Q35, Q36, Q37, Q38, Q39, Q40, Q41, Q42, Q43, Q44, Q45, Q46, Q47, Q48, Q49, Q50, Q51, Q52, Q53, Q54, Q55, Q56, Q57, Q58, Q59, Q60, Q61, Q62, Q63, Q64, Q65, Q66, Q67, Q68, Q69, Q70, Q71, Q72, Q73, Q74]), "depth" : 8 * mm, "offsetDistance" : 25 * mm});
        }
        {
            var Q0;
            Q0=makeQuery(id+"F1.opExtrude","CAP_EDGE",EDGE,{"disambiguationData":[OSD([sQuery(id+"F0.wireOp",EDGE,"E6")])],"isStart":false});
            var Q1;
            Q1=makeQuery(id+"F1.opExtrude","CAP_EDGE",EDGE,{"disambiguationData":[OSD([sQuery(id+"F0.wireOp",EDGE,"E12")])],"isStart":false});
            var Q2;
            Q2=makeQuery(id+"F1.opExtrude","CAP_EDGE",EDGE,{"disambiguationData":[OSD([sQuery(id+"F0.wireOp",EDGE,"E7")])],"isStart":false});
            var Q3;
            Q3=makeQuery(id+"F1.opExtrude","CAP_EDGE",EDGE,{"disambiguationData":[OSD([sQuery(id+"F0.wireOp",EDGE,"E8")])],"isStart":false});
            var Q4;
            Q4=makeQuery(id+"F1.opExtrude","CAP_EDGE",EDGE,{"disambiguationData":[OSD([sQuery(id+"F0.wireOp",EDGE,"E7")])],"isStart":true});
            var Q5;
            Q5=makeQuery(id+"F1.opExtrude","CAP_EDGE",EDGE,{"disambiguationData":[OSD([sQuery(id+"F0.wireOp",EDGE,"E12")])],"isStart":true});
            var Q6;
            Q6=makeQuery(id+"F1.opExtrude","CAP_EDGE",EDGE,{"disambiguationData":[OSD([sQuery(id+"F0.wireOp",EDGE,"E6")])],"isStart":true});
            var Q7;
            Q7=makeQuery(id+"F1.opExtrude","CAP_EDGE",EDGE,{"disambiguationData":[OSD([sQuery(id+"F0.wireOp",EDGE,"E8")])],"isStart":true});
            chamfer(context, id + "F2", {"entities" : qUnion([Q0, Q1, Q2, Q3, Q4, Q5, Q6, Q7]), "width" : 1 * mm, "tangentPropagation" : true});
        }
        {
            var Q0;
            {var subQ0=sQuery(id+"F0.wireOp",EDGE,"E15");Q0=makeQuery(id+"F1.opExtrude","CAP_EDGE",EDGE,{"disambiguationData":[OSD([subQ0]),TDD([makeQuery(id+"F0.imprint","IMPRINT",EDGE,{"disambiguationData":[TD([[makeQuery(id+"F0.imprint","INTERSECT",VERTEX,{"disambiguationData":[OD(0.0)],"derivedFrom":[sQuery(id+"F0.wireOp",EDGE,"E10"),subQ0]}),-1.0]])],"derivedFrom":subQ0}),makeQuery(id+"F0.imprint","IMPRINT",EDGE,{"disambiguationData":[TD([[makeQuery(id+"F0.imprint","INTERSECT",VERTEX,{"disambiguationData":[OD(0.0)],"derivedFrom":[sQuery(id+"F0.wireOp",EDGE,"E9"),subQ0]}),1.0]])],"derivedFrom":subQ0})])],"isStart":true});}
            var Q1;
            {var subQ0=sQuery(id+"F0.wireOp",EDGE,"E15");Q1=makeQuery(id+"F1.opExtrude","CAP_EDGE",EDGE,{"disambiguationData":[OSD([subQ0]),TDD([makeQuery(id+"F0.imprint","IMPRINT",EDGE,{"disambiguationData":[TD([[makeQuery(id+"F0.imprint","INTERSECT",VERTEX,{"disambiguationData":[OD(0.0)],"derivedFrom":[sQuery(id+"F0.wireOp",EDGE,"E10"),subQ0]}),-1.0]])],"derivedFrom":subQ0}),makeQuery(id+"F0.imprint","IMPRINT",EDGE,{"disambiguationData":[TD([[makeQuery(id+"F0.imprint","INTERSECT",VERTEX,{"disambiguationData":[OD(0.0)],"derivedFrom":[sQuery(id+"F0.wireOp",EDGE,"E9"),subQ0]}),1.0]])],"derivedFrom":subQ0})])],"isStart":false});}
            var Q2;
            {var subQ0=sQuery(id+"F0.wireOp",EDGE,"E0");var subQ1=makeQuery(id+"F0.imprint","INTERSECT",VERTEX,{"derivedFrom":[subQ0,sQuery(id+"F0.wireOp",EDGE,"E13")]});Q2=makeQuery(id+"F1.opExtrude","CAP_EDGE",EDGE,{"disambiguationData":[OSD([subQ0]),TDD([makeQuery(id+"F0.imprint","IMPRINT",EDGE,{"disambiguationData":[TD([[makeQuery(id+"F0.imprint","INTERSECT",VERTEX,{"disambiguationData":[OD(1.0)],"derivedFrom":[subQ0,sQuery(id+"F0.wireOp",EDGE,"E11")]}),-1.0]])],"derivedFrom":subQ0}),makeQuery(id+"F0.imprint","IMPRINT",EDGE,{"disambiguationData":[TD([[subQ1,-1.0]])],"derivedFrom":subQ0})])],"isStart":false});}
            var Q3;
            {var subQ0=sQuery(id+"F0.wireOp",EDGE,"E0");var subQ1=makeQuery(id+"F0.imprint","INTERSECT",VERTEX,{"derivedFrom":[subQ0,sQuery(id+"F0.wireOp",EDGE,"E13")]});Q3=makeQuery(id+"F1.opExtrude","CAP_EDGE",EDGE,{"disambiguationData":[OSD([subQ0]),TDD([makeQuery(id+"F0.imprint","IMPRINT",EDGE,{"disambiguationData":[TD([[makeQuery(id+"F0.imprint","INTERSECT",VERTEX,{"disambiguationData":[OD(1.0)],"derivedFrom":[subQ0,sQuery(id+"F0.wireOp",EDGE,"E11")]}),-1.0]])],"derivedFrom":subQ0}),makeQuery(id+"F0.imprint","IMPRINT",EDGE,{"disambiguationData":[TD([[subQ1,-1.0]])],"derivedFrom":subQ0})])],"isStart":true});}
            var Q4;
            {var subQ0=sQuery(id+"F0.wireOp",EDGE,"E0");var subQ1=makeQuery(id+"F0.imprint","INTERSECT",VERTEX,{"derivedFrom":[subQ0,sQuery(id+"F0.wireOp",EDGE,"E14")]});Q4=makeQuery(id+"F1.opExtrude","CAP_EDGE",EDGE,{"disambiguationData":[OSD([subQ0]),TDD([makeQuery(id+"F0.imprint","IMPRINT",EDGE,{"disambiguationData":[TD([[makeQuery(id+"F0.imprint","INTERSECT",VERTEX,{"disambiguationData":[OD(1.0)],"derivedFrom":[subQ0,sQuery(id+"F0.wireOp",EDGE,"E9")]}),-1.0]])],"derivedFrom":subQ0}),makeQuery(id+"F0.imprint","IMPRINT",EDGE,{"disambiguationData":[TD([[subQ1,-1.0]])],"derivedFrom":subQ0})])],"isStart":true});}
            var Q5;
            {var subQ0=sQuery(id+"F0.wireOp",EDGE,"E0");var subQ1=makeQuery(id+"F0.imprint","INTERSECT",VERTEX,{"derivedFrom":[subQ0,sQuery(id+"F0.wireOp",EDGE,"E14")]});Q5=makeQuery(id+"F1.opExtrude","CAP_EDGE",EDGE,{"disambiguationData":[OSD([subQ0]),TDD([makeQuery(id+"F0.imprint","IMPRINT",EDGE,{"disambiguationData":[TD([[makeQuery(id+"F0.imprint","INTERSECT",VERTEX,{"disambiguationData":[OD(1.0)],"derivedFrom":[subQ0,sQuery(id+"F0.wireOp",EDGE,"E9")]}),-1.0]])],"derivedFrom":subQ0}),makeQuery(id+"F0.imprint","IMPRINT",EDGE,{"disambiguationData":[TD([[subQ1,-1.0]])],"derivedFrom":subQ0})])],"isStart":false});}
            fillet(context, id + "F3", {"entities" : qUnion([Q0, Q1, Q2, Q3, Q4, Q5]), "radius" : 4 * mm, "tangentPropagation" : true, "allowEdgeOverflow" : false});
        }
        {
            var Q0;
            {var subQ0=sQuery(id+"F0.wireOp",EDGE,"E19");var subQ1=sQuery(id+"F0.wireOp",EDGE,"E9");Q0=makeQuery(id+"F1.opExtrude","SWEPT_EDGE",EDGE,{"disambiguationData":[OSD([subQ1,subQ0]),TDD([makeQuery(id+"F0.imprint","INTERSECT",VERTEX,{"disambiguationData":[OD(1.0)],"derivedFrom":[subQ1,subQ0]})])]});}
            var Q1;
            {var subQ0=sQuery(id+"F0.wireOp",EDGE,"E19");var subQ1=sQuery(id+"F0.wireOp",EDGE,"E10");Q1=makeQuery(id+"F1.opExtrude","SWEPT_EDGE",EDGE,{"disambiguationData":[OSD([subQ1,subQ0]),TDD([makeQuery(id+"F0.imprint","INTERSECT",VERTEX,{"disambiguationData":[OD(0.0)],"derivedFrom":[subQ1,subQ0]})])]});}
            var Q2;
            {var subQ0=sQuery(id+"F0.wireOp",EDGE,"E19");var subQ1=sQuery(id+"F0.wireOp",EDGE,"E11");Q2=makeQuery(id+"F1.opExtrude","SWEPT_EDGE",EDGE,{"disambiguationData":[OSD([subQ1,subQ0]),TDD([makeQuery(id+"F0.imprint","INTERSECT",VERTEX,{"disambiguationData":[OD(0.0)],"derivedFrom":[subQ1,subQ0]})])]});}
            fillet(context, id + "F4", {"entities" : qUnion([Q0, Q1, Q2]), "radius" : 5 * mm, "tangentPropagation" : true, "allowEdgeOverflow" : false});
        }
        {
            var Q0;
            {var subQ0=sQuery(id+"F0.wireOp",EDGE,"E15");var subQ1=sQuery(id+"F0.wireOp",EDGE,"E9");var subQ2=makeQuery(id+"F0.imprint","INTERSECT",VERTEX,{"disambiguationData":[OD(0.0)],"derivedFrom":[subQ1,subQ0]});Q0=makeQuery(id+"F3.opFillet","BLEND_EDGE",EDGE,{"blendedFrom":[makeQuery(id+"F1.opExtrude","CAP_EDGE",EDGE,{"disambiguationData":[OSD([subQ0]),TDD([makeQuery(id+"F0.imprint","IMPRINT",EDGE,{"disambiguationData":[TD([[makeQuery(id+"F0.imprint","INTERSECT",VERTEX,{"disambiguationData":[OD(0.0)],"derivedFrom":[sQuery(id+"F0.wireOp",EDGE,"E10"),subQ0]}),-1.0]])],"derivedFrom":subQ0}),makeQuery(id+"F0.imprint","IMPRINT",EDGE,{"disambiguationData":[TD([[subQ2,1.0]])],"derivedFrom":subQ0})])],"isStart":false}),makeQuery(id+"F1.opExtrude","SWEPT_FACE",FACE,{"disambiguationData":[OSD([subQ1]),TDD([makeQuery(id+"F0.imprint","IMPRINT",EDGE,{"disambiguationData":[TD([[subQ2,-1.0]])],"derivedFrom":subQ1})])]})],"blendedInto":[makeQuery(id+"F1.opExtrude","SWEPT_FACE",FACE,{"disambiguationData":[OSD([subQ1]),TDD([makeQuery(id+"F0.imprint","IMPRINT",EDGE,{"disambiguationData":[TD([[subQ2,-1.0]])],"derivedFrom":subQ1})])]})]});}
            var Q1;
            {var subQ0=sQuery(id+"F0.wireOp",EDGE,"E10");var subQ1=sQuery(id+"F0.wireOp",EDGE,"E15");var subQ2=makeQuery(id+"F0.imprint","INTERSECT",VERTEX,{"disambiguationData":[OD(0.0)],"derivedFrom":[subQ0,subQ1]});Q1=makeQuery(id+"F3.opFillet","BLEND_EDGE",EDGE,{"blendedFrom":[makeQuery(id+"F1.opExtrude","CAP_EDGE",EDGE,{"disambiguationData":[OSD([subQ1]),TDD([makeQuery(id+"F0.imprint","IMPRINT",EDGE,{"disambiguationData":[TD([[subQ2,-1.0]])],"derivedFrom":subQ1}),makeQuery(id+"F0.imprint","IMPRINT",EDGE,{"disambiguationData":[TD([[makeQuery(id+"F0.imprint","INTERSECT",VERTEX,{"disambiguationData":[OD(0.0)],"derivedFrom":[sQuery(id+"F0.wireOp",EDGE,"E9"),subQ1]}),1.0]])],"derivedFrom":subQ1})])],"isStart":false}),makeQuery(id+"F1.opExtrude","SWEPT_FACE",FACE,{"disambiguationData":[OSD([subQ0]),TDD([makeQuery(id+"F0.imprint","IMPRINT",EDGE,{"disambiguationData":[TD([[makeQuery(id+"F0.imprint","INTERSECT",VERTEX,{"disambiguationData":[OD(0.0)],"derivedFrom":[subQ0,sQuery(id+"F0.wireOp",EDGE,"E19")]}),-1.0]])],"derivedFrom":subQ0})])]})],"blendedInto":[makeQuery(id+"F1.opExtrude","SWEPT_FACE",FACE,{"disambiguationData":[OSD([subQ0]),TDD([makeQuery(id+"F0.imprint","IMPRINT",EDGE,{"disambiguationData":[TD([[makeQuery(id+"F0.imprint","INTERSECT",VERTEX,{"disambiguationData":[OD(0.0)],"derivedFrom":[subQ0,sQuery(id+"F0.wireOp",EDGE,"E19")]}),-1.0]])],"derivedFrom":subQ0})])]})]});}
            var Q2;
            {var subQ0=sQuery(id+"F0.wireOp",EDGE,"E13");var subQ1=sQuery(id+"F0.wireOp",EDGE,"E10");var subQ2=makeQuery(id+"F0.imprint","INTERSECT",VERTEX,{"disambiguationData":[OD(1.0)],"derivedFrom":[subQ1,subQ0]});var subQ3=sQuery(id+"F0.wireOp",EDGE,"E0");var subQ4=makeQuery(id+"F0.imprint","INTERSECT",VERTEX,{"disambiguationData":[OD(1.0)],"derivedFrom":[subQ3,subQ1]});var subQ5=makeQuery(id+"F0.imprint","INTERSECT",VERTEX,{"derivedFrom":[subQ3,subQ0]});Q2=makeQuery(id+"F3.opFillet","BLEND_EDGE",EDGE,{"blendedFrom":[makeQuery(id+"F1.opExtrude","CAP_EDGE",EDGE,{"disambiguationData":[OSD([subQ3]),TDD([makeQuery(id+"F0.imprint","IMPRINT",EDGE,{"disambiguationData":[TD([[makeQuery(id+"F0.imprint","INTERSECT",VERTEX,{"disambiguationData":[OD(1.0)],"derivedFrom":[subQ3,sQuery(id+"F0.wireOp",EDGE,"E11")]}),-1.0]])],"derivedFrom":subQ3}),makeQuery(id+"F0.imprint","IMPRINT",EDGE,{"disambiguationData":[TD([[subQ5,-1.0]])],"derivedFrom":subQ3})])],"isStart":true}),makeQuery(id+"F1.opExtrude","SWEPT_FACE",FACE,{"disambiguationData":[OSD([subQ1]),TDD([makeQuery(id+"F0.imprint","IMPRINT",EDGE,{"disambiguationData":[TD([[subQ4,-1.0]])],"derivedFrom":subQ1}),makeQuery(id+"F0.imprint","IMPRINT",EDGE,{"disambiguationData":[TD([[subQ2,-1.0]])],"derivedFrom":subQ1})])]})],"blendedInto":[makeQuery(id+"F1.opExtrude","SWEPT_FACE",FACE,{"disambiguationData":[OSD([subQ1]),TDD([makeQuery(id+"F0.imprint","IMPRINT",EDGE,{"disambiguationData":[TD([[subQ4,-1.0]])],"derivedFrom":subQ1}),makeQuery(id+"F0.imprint","IMPRINT",EDGE,{"disambiguationData":[TD([[subQ2,-1.0]])],"derivedFrom":subQ1})])]})]});}
            var Q3;
            {var subQ0=sQuery(id+"F0.wireOp",EDGE,"E11");var subQ1=sQuery(id+"F0.wireOp",EDGE,"E0");var subQ2=makeQuery(id+"F0.imprint","INTERSECT",VERTEX,{"disambiguationData":[OD(1.0)],"derivedFrom":[subQ1,subQ0]});var subQ3=sQuery(id+"F0.wireOp",EDGE,"E13");var subQ5=makeQuery(id+"F0.imprint","INTERSECT",VERTEX,{"disambiguationData":[OD(0.0)],"derivedFrom":[subQ0,sQuery(id+"F0.wireOp",EDGE,"E16")]});var subQ6=makeQuery(id+"F0.imprint","INTERSECT",VERTEX,{"derivedFrom":[subQ1,subQ3]});Q3=makeQuery(id+"F3.opFillet","BLEND_EDGE",EDGE,{"blendedFrom":[makeQuery(id+"F1.opExtrude","CAP_EDGE",EDGE,{"disambiguationData":[OSD([subQ1]),TDD([makeQuery(id+"F0.imprint","IMPRINT",EDGE,{"disambiguationData":[TD([[subQ2,-1.0]])],"derivedFrom":subQ1}),makeQuery(id+"F0.imprint","IMPRINT",EDGE,{"disambiguationData":[TD([[subQ6,-1.0]])],"derivedFrom":subQ1})])],"isStart":true}),makeQuery(id+"F1.opExtrude","SWEPT_FACE",FACE,{"disambiguationData":[OSD([subQ0]),TDD([makeQuery(id+"F0.imprint","IMPRINT",EDGE,{"disambiguationData":[TD([[makeQuery(id+"F0.imprint","INTERSECT",VERTEX,{"disambiguationData":[OD(0.0)],"derivedFrom":[subQ0,sQuery(id+"F0.wireOp",EDGE,"E19")]}),-1.0]])],"derivedFrom":subQ0}),makeQuery(id+"F0.imprint","IMPRINT",EDGE,{"disambiguationData":[TD([[subQ5,-1.0]])],"derivedFrom":subQ0}),makeQuery(id+"F0.imprint","IMPRINT",EDGE,{"disambiguationData":[TD([[subQ2,1.0]])],"derivedFrom":subQ0})])]})],"blendedInto":[makeQuery(id+"F1.opExtrude","SWEPT_FACE",FACE,{"disambiguationData":[OSD([subQ0]),TDD([makeQuery(id+"F0.imprint","IMPRINT",EDGE,{"disambiguationData":[TD([[makeQuery(id+"F0.imprint","INTERSECT",VERTEX,{"disambiguationData":[OD(0.0)],"derivedFrom":[subQ0,sQuery(id+"F0.wireOp",EDGE,"E19")]}),-1.0]])],"derivedFrom":subQ0}),makeQuery(id+"F0.imprint","IMPRINT",EDGE,{"disambiguationData":[TD([[subQ5,-1.0]])],"derivedFrom":subQ0}),makeQuery(id+"F0.imprint","IMPRINT",EDGE,{"disambiguationData":[TD([[subQ2,1.0]])],"derivedFrom":subQ0})])]})]});}
            var Q4;
            {var subQ0=sQuery(id+"F0.wireOp",EDGE,"E9");var subQ1=sQuery(id+"F0.wireOp",EDGE,"E0");var subQ2=makeQuery(id+"F0.imprint","INTERSECT",VERTEX,{"disambiguationData":[OD(1.0)],"derivedFrom":[subQ1,subQ0]});var subQ3=sQuery(id+"F0.wireOp",EDGE,"E14");var subQ5=makeQuery(id+"F0.imprint","INTERSECT",VERTEX,{"derivedFrom":[subQ1,subQ3]});Q4=makeQuery(id+"F3.opFillet","BLEND_EDGE",EDGE,{"blendedFrom":[makeQuery(id+"F1.opExtrude","CAP_EDGE",EDGE,{"disambiguationData":[OSD([subQ1]),TDD([makeQuery(id+"F0.imprint","IMPRINT",EDGE,{"disambiguationData":[TD([[subQ2,-1.0]])],"derivedFrom":subQ1}),makeQuery(id+"F0.imprint","IMPRINT",EDGE,{"disambiguationData":[TD([[subQ5,-1.0]])],"derivedFrom":subQ1})])],"isStart":true}),makeQuery(id+"F1.opExtrude","SWEPT_FACE",FACE,{"disambiguationData":[OSD([subQ0]),TDD([makeQuery(id+"F0.imprint","IMPRINT",EDGE,{"disambiguationData":[TD([[makeQuery(id+"F0.imprint","INTERSECT",VERTEX,{"disambiguationData":[OD(1.0)],"derivedFrom":[subQ0,sQuery(id+"F0.wireOp",EDGE,"E19")]}),-1.0]])],"derivedFrom":subQ0}),makeQuery(id+"F0.imprint","IMPRINT",EDGE,{"disambiguationData":[TD([[subQ2,1.0]])],"derivedFrom":subQ0})])]})],"blendedInto":[makeQuery(id+"F1.opExtrude","SWEPT_FACE",FACE,{"disambiguationData":[OSD([subQ0]),TDD([makeQuery(id+"F0.imprint","IMPRINT",EDGE,{"disambiguationData":[TD([[makeQuery(id+"F0.imprint","INTERSECT",VERTEX,{"disambiguationData":[OD(1.0)],"derivedFrom":[subQ0,sQuery(id+"F0.wireOp",EDGE,"E19")]}),-1.0]])],"derivedFrom":subQ0}),makeQuery(id+"F0.imprint","IMPRINT",EDGE,{"disambiguationData":[TD([[subQ2,1.0]])],"derivedFrom":subQ0})])]})]});}
            var Q5;
            {var subQ0=sQuery(id+"F0.wireOp",EDGE,"E11");var subQ1=makeQuery(id+"F0.imprint","INTERSECT",VERTEX,{"disambiguationData":[OD(1.0)],"derivedFrom":[subQ0,sQuery(id+"F0.wireOp",EDGE,"E16")]});var subQ2=sQuery(id+"F0.wireOp",EDGE,"E14");var subQ3=makeQuery(id+"F0.imprint","INTERSECT",VERTEX,{"disambiguationData":[OD(1.0)],"derivedFrom":[subQ0,subQ2]});var subQ4=sQuery(id+"F0.wireOp",EDGE,"E0");var subQ5=makeQuery(id+"F0.imprint","INTERSECT",VERTEX,{"disambiguationData":[OD(0.0)],"derivedFrom":[subQ4,subQ0]});var subQ6=makeQuery(id+"F0.imprint","INTERSECT",VERTEX,{"derivedFrom":[subQ4,subQ2]});Q5=makeQuery(id+"F3.opFillet","BLEND_EDGE",EDGE,{"blendedFrom":[makeQuery(id+"F1.opExtrude","CAP_EDGE",EDGE,{"disambiguationData":[OSD([subQ4]),TDD([makeQuery(id+"F0.imprint","IMPRINT",EDGE,{"disambiguationData":[TD([[makeQuery(id+"F0.imprint","INTERSECT",VERTEX,{"disambiguationData":[OD(1.0)],"derivedFrom":[subQ4,sQuery(id+"F0.wireOp",EDGE,"E9")]}),-1.0]])],"derivedFrom":subQ4}),makeQuery(id+"F0.imprint","IMPRINT",EDGE,{"disambiguationData":[TD([[subQ6,-1.0]])],"derivedFrom":subQ4})])],"isStart":true}),makeQuery(id+"F1.opExtrude","SWEPT_FACE",FACE,{"disambiguationData":[OSD([subQ0]),TDD([makeQuery(id+"F0.imprint","IMPRINT",EDGE,{"disambiguationData":[TD([[subQ5,-1.0]])],"derivedFrom":subQ0}),makeQuery(id+"F0.imprint","IMPRINT",EDGE,{"disambiguationData":[TD([[subQ3,-1.0]])],"derivedFrom":subQ0}),makeQuery(id+"F0.imprint","IMPRINT",EDGE,{"disambiguationData":[TD([[subQ1,-1.0]])],"derivedFrom":subQ0})])]})],"blendedInto":[makeQuery(id+"F1.opExtrude","SWEPT_FACE",FACE,{"disambiguationData":[OSD([subQ0]),TDD([makeQuery(id+"F0.imprint","IMPRINT",EDGE,{"disambiguationData":[TD([[subQ5,-1.0]])],"derivedFrom":subQ0}),makeQuery(id+"F0.imprint","IMPRINT",EDGE,{"disambiguationData":[TD([[subQ3,-1.0]])],"derivedFrom":subQ0}),makeQuery(id+"F0.imprint","IMPRINT",EDGE,{"disambiguationData":[TD([[subQ1,-1.0]])],"derivedFrom":subQ0})])]})]});}
            fillet(context, id + "F5", {"entities" : qUnion([Q0, Q1, Q2, Q3, Q4, Q5]), "radius" : 5 * mm, "tangentPropagation" : true, "allowEdgeOverflow" : false});
        }
    });
